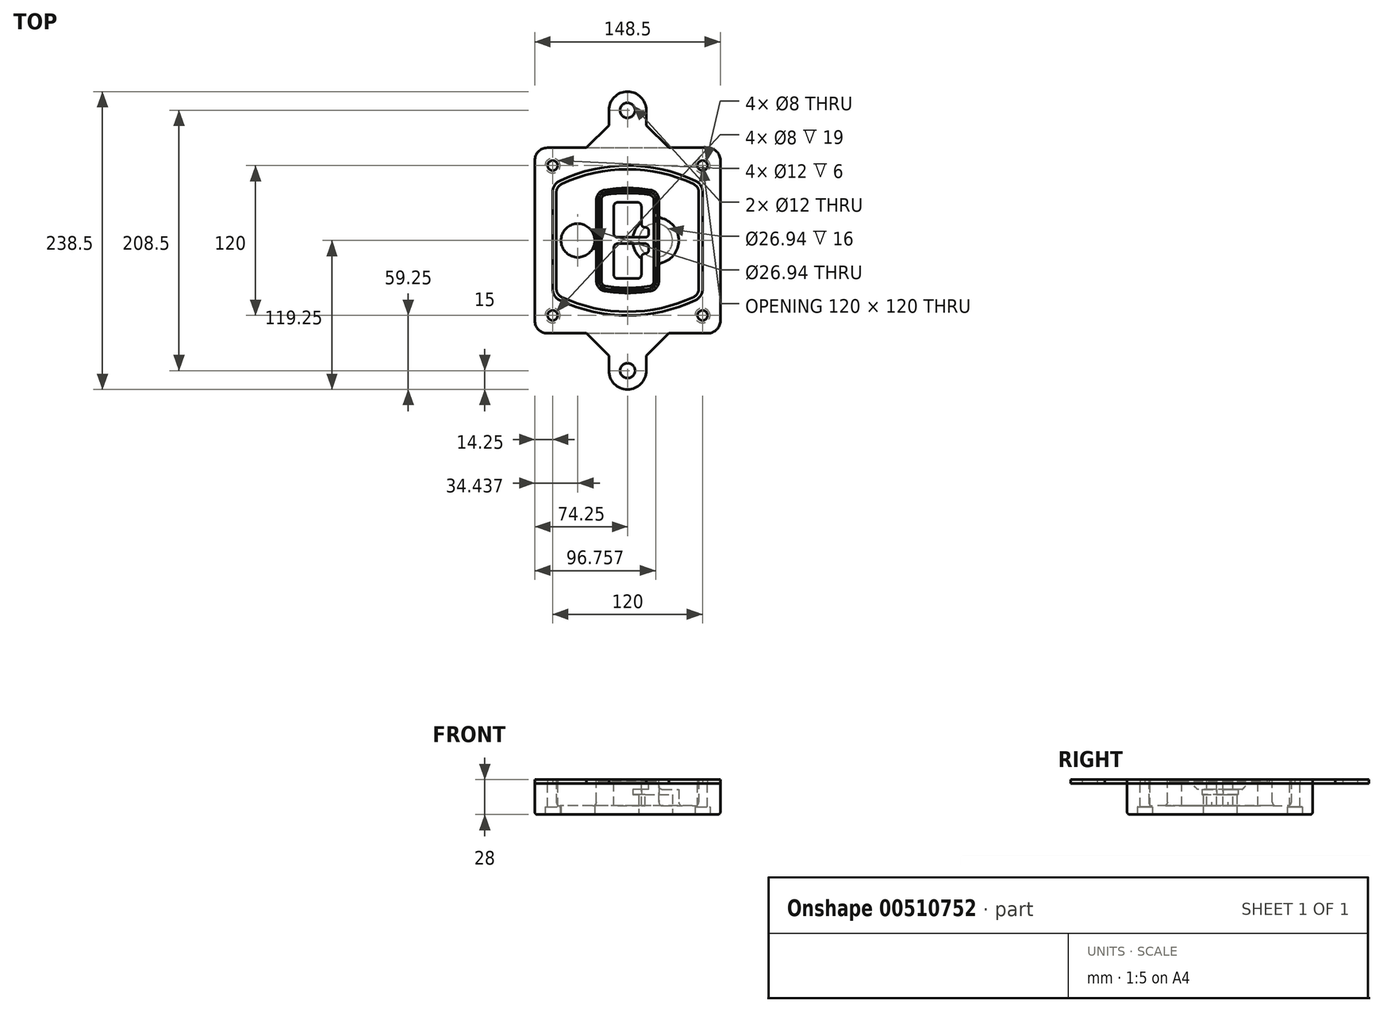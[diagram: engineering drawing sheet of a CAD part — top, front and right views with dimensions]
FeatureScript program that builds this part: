
annotation { "Feature Type Name" : "Feature", "Feature Type Description" : "" }
export const myFeature = defineFeature(function(context is Context, id is Id, definition is map)
    precondition{}
    {
        {
            var Q0;
            Q0=qCreatedBy(makeId("Top.planeOp"),FACE);
            var sketch = newSketch(context, id + "F0", { "sketchPlane" : qUnion([Q0])});
            skPoint(sketch, "E0.rect.middle", {"position": v(0, 0) * mm});
            skLineSegment(sketch, "E1.bottom", {"start": v(-64.25, -74.25) * mm, "end": v(64.25, -74.25) * mm});
            skLineSegment(sketch, "E1.top", {"start": v(-64.25, 74.25) * mm, "end": v(64.25, 74.25) * mm});
            skLineSegment(sketch, "E1.left", {"start": v(-74.25, -64.25) * mm, "end": v(-74.25, 64.25) * mm});
            skLineSegment(sketch, "E1.right", {"start": v(74.25, -64.25) * mm, "end": v(74.25, 64.25) * mm});
            skLineSegment(sketch, "E2", {"start": v(-74.25, 74.25) * mm, "end": v(74.25, -74.25) * mm, "construction": true});
            skLineSegment(sketch, "E3", {"start": v(74.25, 74.25) * mm, "end": v(-74.25, -74.25) * mm, "construction": true});
            skCircle(sketch, "E4", {"center": v(-60, 60) * mm, "radius": 4 * mm});
            skCircle(sketch, "E5", {"center": v(60, 60) * mm, "radius": 4 * mm});
            skCircle(sketch, "E6", {"center": v(60, -60) * mm, "radius": 4 * mm});
            skCircle(sketch, "E7", {"center": v(-60, -60) * mm, "radius": 4 * mm});
            skLineSegment(sketch, "E8", {"start": v(-60, 60) * mm, "end": v(60, 60) * mm, "construction": true});
            skLineSegment(sketch, "E9", {"start": v(60, 60) * mm, "end": v(60, -60) * mm, "construction": true});
            skLineSegment(sketch, "E10", {"start": v(60, -60) * mm, "end": v(-60, -60) * mm, "construction": true});
            skLineSegment(sketch, "E11", {"start": v(-60, -60) * mm, "end": v(-60, 60) * mm, "construction": true});
            skLineSegment(sketch, "E12", {"start": v(-60, 38.83) * mm, "end": v(-60, -38.83) * mm});
            skLineSegment(sketch, "E13", {"start": v(60, 38.83) * mm, "end": v(60, -38.83) * mm});
            skArc(sketch, "E14", {"start": v(54.26, 47.88) * mm, "mid": v(0, 60) * mm, "end": v(-54.26, 47.88) * mm});
            skArc(sketch, "E15", {"start": v(-54.26, -47.88) * mm, "mid": v(0, -60) * mm, "end": v(54.26, -47.88) * mm});
            skLineSegment(sketch, "E16", {"start": v(-60, 0) * mm, "end": v(60, 0) * mm, "construction": true});
            skPoint(sketch, "E17.visualSharp", {"position": v(-60, -45) * mm});
            skArc(sketch, "E17.filletArc", {"start": v(-60, -38.83) * mm, "mid": v(-58.44, -44.2) * mm, "end": v(-54.26, -47.88) * mm});
            skPoint(sketch, "E18.visualSharp", {"position": v(-60, 45) * mm});
            skArc(sketch, "E18.filletArc", {"start": v(-54.26, 47.88) * mm, "mid": v(-58.44, 44.2) * mm, "end": v(-60, 38.83) * mm});
            skPoint(sketch, "E19.visualSharp", {"position": v(60, 45) * mm});
            skArc(sketch, "E19.filletArc", {"start": v(60, 38.83) * mm, "mid": v(58.44, 44.2) * mm, "end": v(54.26, 47.88) * mm});
            skPoint(sketch, "E20.visualSharp", {"position": v(60, -45) * mm});
            skArc(sketch, "E20.filletArc", {"start": v(54.26, -47.88) * mm, "mid": v(58.44, -44.2) * mm, "end": v(60, -38.83) * mm});
            skPoint(sketch, "E21.visualSharp", {"position": v(-74.25, 74.25) * mm});
            skArc(sketch, "E21.filletArc", {"start": v(-64.25, 74.25) * mm, "mid": v(-71.32, 71.32) * mm, "end": v(-74.25, 64.25) * mm});
            skPoint(sketch, "E22.visualSharp", {"position": v(74.25, 74.25) * mm});
            skArc(sketch, "E22.filletArc", {"start": v(74.25, 64.25) * mm, "mid": v(71.32, 71.32) * mm, "end": v(64.25, 74.25) * mm});
            skPoint(sketch, "E23.visualSharp", {"position": v(74.25, -74.25) * mm});
            skArc(sketch, "E23.filletArc", {"start": v(64.25, -74.25) * mm, "mid": v(71.32, -71.32) * mm, "end": v(74.25, -64.25) * mm});
            skPoint(sketch, "E24.visualSharp", {"position": v(-74.25, -74.25) * mm});
            skArc(sketch, "E24.filletArc", {"start": v(-74.25, -64.25) * mm, "mid": v(-71.32, -71.32) * mm, "end": v(-64.25, -74.25) * mm});
            skArc(sketch, "E25.0", {"start": v(57, 38.83) * mm, "mid": v(55.9, 42.58) * mm, "end": v(52.98, 45.17) * mm});
            skLineSegment(sketch, "E25.1", {"start": v(57, 38.83) * mm, "end": v(57, -38.83) * mm});
            skArc(sketch, "E25.2", {"start": v(52.98, -45.17) * mm, "mid": v(55.9, -42.58) * mm, "end": v(57, -38.83) * mm});
            skArc(sketch, "E25.3", {"start": v(-52.98, -45.17) * mm, "mid": v(0, -57) * mm, "end": v(52.98, -45.17) * mm});
            skArc(sketch, "E25.4", {"start": v(-57, -38.83) * mm, "mid": v(-55.9, -42.58) * mm, "end": v(-52.98, -45.17) * mm});
            skArc(sketch, "E25.5", {"start": v(52.98, 45.17) * mm, "mid": v(0, 57) * mm, "end": v(-52.98, 45.17) * mm});
            skLineSegment(sketch, "E25.6", {"start": v(-57, 38.83) * mm, "end": v(-57, -38.83) * mm});
            skArc(sketch, "E25.7", {"start": v(-52.98, 45.17) * mm, "mid": v(-55.9, 42.58) * mm, "end": v(-57, 38.83) * mm});
            skArc(sketch, "E26.0", {"start": v(-55.96, 51.5) * mm, "mid": v(-61.82, 46.33) * mm, "end": v(-64, 38.83) * mm});
            skArc(sketch, "E26.1", {"start": v(55.96, 51.5) * mm, "mid": v(0, 64) * mm, "end": v(-55.96, 51.5) * mm});
            skArc(sketch, "E26.2", {"start": v(64, 38.83) * mm, "mid": v(61.82, 46.33) * mm, "end": v(55.96, 51.5) * mm});
            skLineSegment(sketch, "E26.3", {"start": v(64, 38.83) * mm, "end": v(64, -38.83) * mm});
            skArc(sketch, "E26.4", {"start": v(55.96, -51.5) * mm, "mid": v(61.82, -46.33) * mm, "end": v(64, -38.83) * mm});
            skLineSegment(sketch, "E26.5", {"start": v(-64, 38.83) * mm, "end": v(-64, -38.83) * mm});
            skArc(sketch, "E26.6", {"start": v(-55.96, -51.5) * mm, "mid": v(0, -64) * mm, "end": v(55.96, -51.5) * mm});
            skArc(sketch, "E26.7", {"start": v(-64, -38.83) * mm, "mid": v(-61.82, -46.33) * mm, "end": v(-55.96, -51.5) * mm});
            skSolve(sketch);
        }
        {
            var Q0;
            Q0=makeQuery(id+"F0.imprint","IMPRINT",FACE,{"disambiguationData":[TD([[makeQuery(id+"F0.imprint","IMPRINT",EDGE,{"derivedFrom":sQuery(id+"F0.wireOp",EDGE,"E1.bottom")}),1.0]])]});
            var Q1;
            Q1=makeQuery(id+"F0.imprint","IMPRINT",FACE,{"disambiguationData":[TD([[makeQuery(id+"F0.imprint","IMPRINT",EDGE,{"derivedFrom":sQuery(id+"F0.wireOp",EDGE,"E12")}),1.0]])]});
            var Q2;
            Q2=makeQuery(id+"F0.imprint","IMPRINT",FACE,{"disambiguationData":[TD([[makeQuery(id+"F0.imprint","IMPRINT",EDGE,{"derivedFrom":sQuery(id+"F0.wireOp",EDGE,"E25.0")}),1.0]])]});
            var Q3;
            Q3=makeQuery(id+"F0.imprint","IMPRINT",FACE,{"disambiguationData":[TD([[makeQuery(id+"F0.imprint","IMPRINT",EDGE,{"derivedFrom":sQuery(id+"F0.wireOp",EDGE,"E12")}),-1.0]])]});
            extrude(context, id + "F1", {"entities" : qUnion([Q0, Q1, Q2, Q3]), "oppositeDirection" : true, "depth" : 25 * mm});
        }
        {
            var Q0;
            Q0=makeQuery(id+"F0.imprint","IMPRINT",FACE,{"disambiguationData":[TD([[makeQuery(id+"F0.imprint","IMPRINT",EDGE,{"derivedFrom":sQuery(id+"F0.wireOp",EDGE,"E12")}),1.0]])]});
            extrude(context, id + "F2", {"entities" : qUnion([Q0]), "operationType" : NewBodyOperationType.ADD, "depth" : 3 * mm});
        }
        {
            var Q0;
            Q0=makeQuery(id+"F0.imprint","IMPRINT",FACE,{"disambiguationData":[TD([[makeQuery(id+"F0.imprint","IMPRINT",EDGE,{"derivedFrom":sQuery(id+"F0.wireOp",EDGE,"E25.0")}),1.0]])]});
            extrude(context, id + "F3", {"entities" : qUnion([Q0]), "operationType" : NewBodyOperationType.REMOVE, "oppositeDirection" : true, "depth" : 18 * mm});
        }
        {
            var Q0;
            Q0=makeQuery(id+"F2.opExtrude","CAP_FACE",FACE,{"disambiguationData":[OSD([sQuery(id+"F0.wireOp",EDGE,"E12"),sQuery(id+"F0.wireOp",EDGE,"E13"),sQuery(id+"F0.wireOp",EDGE,"E14"),sQuery(id+"F0.wireOp",EDGE,"E15"),sQuery(id+"F0.wireOp",EDGE,"E17.filletArc"),sQuery(id+"F0.wireOp",EDGE,"E18.filletArc"),sQuery(id+"F0.wireOp",EDGE,"E19.filletArc"),sQuery(id+"F0.wireOp",EDGE,"E20.filletArc"),sQuery(id+"F0.wireOp",EDGE,"E25.0"),sQuery(id+"F0.wireOp",EDGE,"E25.1"),sQuery(id+"F0.wireOp",EDGE,"E25.2"),sQuery(id+"F0.wireOp",EDGE,"E25.3"),sQuery(id+"F0.wireOp",EDGE,"E25.4"),sQuery(id+"F0.wireOp",EDGE,"E25.5"),sQuery(id+"F0.wireOp",EDGE,"E25.6"),sQuery(id+"F0.wireOp",EDGE,"E25.7")])],"isStart":false});
            var sketch = newSketch(context, id + "F4", { "sketchPlane" : qUnion([Q0])});
            skArc(sketch, "E27.0", {"start": v(-18.34, -40.45) * mm, "mid": v(0, -42) * mm, "end": v(18.34, -40.45) * mm});
            skArc(sketch, "E28.0", {"start": v(18.34, 40.45) * mm, "mid": v(0, 42) * mm, "end": v(-18.34, 40.45) * mm});
            skLineSegment(sketch, "E29", {"start": v(-25, 32.57) * mm, "end": v(-25, -32.57) * mm});
            skLineSegment(sketch, "E30", {"start": v(25, 32.57) * mm, "end": v(25, -32.57) * mm});
            skLineSegment(sketch, "E31", {"start": v(-25, 39.1) * mm, "end": v(25, 39.1) * mm, "construction": true});
            skLineSegment(sketch, "E32", {"start": v(-25, -39.1) * mm, "end": v(25, -39.1) * mm, "construction": true});
            skPoint(sketch, "E33.visualSharp", {"position": v(-25, 39.1) * mm});
            skArc(sketch, "E33.filletArc", {"start": v(-18.34, 40.45) * mm, "mid": v(-23.11, 37.73) * mm, "end": v(-25, 32.57) * mm});
            skPoint(sketch, "E34.visualSharp", {"position": v(25, 39.1) * mm});
            skArc(sketch, "E34.filletArc", {"start": v(25, 32.57) * mm, "mid": v(23.11, 37.73) * mm, "end": v(18.34, 40.45) * mm});
            skPoint(sketch, "E35.visualSharp", {"position": v(25, -39.1) * mm});
            skArc(sketch, "E35.filletArc", {"start": v(18.34, -40.45) * mm, "mid": v(23.11, -37.73) * mm, "end": v(25, -32.57) * mm});
            skPoint(sketch, "E36.visualSharp", {"position": v(-25, -39.1) * mm});
            skArc(sketch, "E36.filletArc", {"start": v(-25, -32.57) * mm, "mid": v(-23.11, -37.73) * mm, "end": v(-18.34, -40.45) * mm});
            skArc(sketch, "E37.0", {"start": v(52.98, 45.17) * mm, "mid": v(0, 57) * mm, "end": v(-52.98, 45.17) * mm});
            skArc(sketch, "E37.1", {"start": v(-52.98, 45.17) * mm, "mid": v(-55.9, 42.58) * mm, "end": v(-57, 38.83) * mm});
            skLineSegment(sketch, "E37.2", {"start": v(-57, 38.83) * mm, "end": v(-57, -38.83) * mm});
            skArc(sketch, "E37.3", {"start": v(-57, -38.83) * mm, "mid": v(-55.9, -42.58) * mm, "end": v(-52.98, -45.17) * mm});
            skArc(sketch, "E37.4", {"start": v(-52.98, -45.17) * mm, "mid": v(0, -57) * mm, "end": v(52.98, -45.17) * mm});
            skArc(sketch, "E37.5", {"start": v(52.98, -45.17) * mm, "mid": v(55.9, -42.58) * mm, "end": v(57, -38.83) * mm});
            skLineSegment(sketch, "E37.6", {"start": v(57, 38.83) * mm, "end": v(57, -38.83) * mm});
            skArc(sketch, "E37.7", {"start": v(57, 38.83) * mm, "mid": v(55.9, 42.58) * mm, "end": v(52.98, 45.17) * mm});
            skLineSegment(sketch, "E38.0", {"start": v(23, 32.57) * mm, "end": v(23, -32.57) * mm});
            skArc(sketch, "E38.1", {"start": v(18, -38.48) * mm, "mid": v(21.58, -36.44) * mm, "end": v(23, -32.57) * mm});
            skArc(sketch, "E38.2", {"start": v(-18, -38.48) * mm, "mid": v(0, -40) * mm, "end": v(18, -38.48) * mm});
            skArc(sketch, "E38.3", {"start": v(-23, -32.57) * mm, "mid": v(-21.58, -36.44) * mm, "end": v(-18, -38.48) * mm});
            skLineSegment(sketch, "E38.4", {"start": v(-23, 32.57) * mm, "end": v(-23, -32.57) * mm});
            skArc(sketch, "E38.5", {"start": v(23, 32.57) * mm, "mid": v(21.58, 36.44) * mm, "end": v(18, 38.48) * mm});
            skArc(sketch, "E38.6", {"start": v(-18, 38.48) * mm, "mid": v(-21.58, 36.44) * mm, "end": v(-23, 32.57) * mm});
            skArc(sketch, "E38.7", {"start": v(18, 38.48) * mm, "mid": v(0, 40) * mm, "end": v(-18, 38.48) * mm});
            skArc(sketch, "E39.0", {"start": v(21, 32.57) * mm, "mid": v(20.06, 35.15) * mm, "end": v(17.67, 36.5) * mm});
            skLineSegment(sketch, "E39.1", {"start": v(21, 32.57) * mm, "end": v(21, -32.57) * mm});
            skArc(sketch, "E39.2", {"start": v(17.67, -36.5) * mm, "mid": v(20.06, -35.15) * mm, "end": v(21, -32.57) * mm});
            skArc(sketch, "E39.3", {"start": v(-17.67, -36.5) * mm, "mid": v(0, -38) * mm, "end": v(17.67, -36.5) * mm});
            skArc(sketch, "E39.4", {"start": v(-21, -32.57) * mm, "mid": v(-20.06, -35.15) * mm, "end": v(-17.67, -36.5) * mm});
            skArc(sketch, "E39.5", {"start": v(17.67, 36.5) * mm, "mid": v(0, 38) * mm, "end": v(-17.67, 36.5) * mm});
            skLineSegment(sketch, "E39.6", {"start": v(-21, 32.57) * mm, "end": v(-21, -32.57) * mm});
            skArc(sketch, "E39.7", {"start": v(-17.67, 36.5) * mm, "mid": v(-20.06, 35.15) * mm, "end": v(-21, 32.57) * mm});
            skLineSegment(sketch, "E40", {"start": v(-25, 0) * mm, "end": v(25, 0) * mm, "construction": true});
            skLineSegment(sketch, "E41", {"start": v(-11, 5.5) * mm, "end": v(-11, 27.5) * mm});
            skLineSegment(sketch, "E42", {"start": v(-8, 30.5) * mm, "end": v(8, 30.5) * mm});
            skLineSegment(sketch, "E43", {"start": v(11, 27.5) * mm, "end": v(11, 13.5) * mm});
            skLineSegment(sketch, "E44", {"start": v(14, 10.5) * mm, "end": v(14, 10.5) * mm});
            skLineSegment(sketch, "E45", {"start": v(17, 7.5) * mm, "end": v(17, 5.5) * mm});
            skLineSegment(sketch, "E46", {"start": v(14, 2.5) * mm, "end": v(-8, 2.5) * mm});
            skPoint(sketch, "E47.visualSharp", {"position": v(-11, 30.5) * mm});
            skArc(sketch, "E47.filletArc", {"start": v(-8, 30.5) * mm, "mid": v(-10.12, 29.62) * mm, "end": v(-11, 27.5) * mm});
            skPoint(sketch, "E48.visualSharp", {"position": v(11, 30.5) * mm});
            skArc(sketch, "E48.filletArc", {"start": v(11, 27.5) * mm, "mid": v(10.12, 29.62) * mm, "end": v(8, 30.5) * mm});
            skPoint(sketch, "E49.visualSharp", {"position": v(11, 10.5) * mm});
            skArc(sketch, "E49.filletArc", {"start": v(11, 13.5) * mm, "mid": v(11.88, 11.38) * mm, "end": v(14, 10.5) * mm});
            skPoint(sketch, "E50.visualSharp", {"position": v(17, 10.5) * mm});
            skArc(sketch, "E50.filletArc", {"start": v(17, 7.5) * mm, "mid": v(16.12, 9.62) * mm, "end": v(14, 10.5) * mm});
            skPoint(sketch, "E51.visualSharp", {"position": v(17, 2.5) * mm});
            skArc(sketch, "E51.filletArc", {"start": v(14, 2.5) * mm, "mid": v(16.12, 3.38) * mm, "end": v(17, 5.5) * mm});
            skPoint(sketch, "E52.visualSharp", {"position": v(-11, 2.5) * mm});
            skArc(sketch, "E52.filletArc", {"start": v(-11, 5.5) * mm, "mid": v(-10.12, 3.38) * mm, "end": v(-8, 2.5) * mm});
            skLineSegment(sketch, "E53.0.MirrorCS", {"start": v(14, -2.5) * mm, "end": v(-8, -2.5) * mm});
            skArc(sketch, "E54.0.MirrorCS", {"start": v(-11, -5.5) * mm, "mid": v(-10.12, -3.38) * mm, "end": v(-8, -2.5) * mm});
            skLineSegment(sketch, "E55.0.MirrorCS", {"start": v(-11, -5.5) * mm, "end": v(-11, -27.5) * mm});
            skArc(sketch, "E56.0.MirrorCS", {"start": v(-8, -30.5) * mm, "mid": v(-10.12, -29.62) * mm, "end": v(-11, -27.5) * mm});
            skLineSegment(sketch, "E57.0.MirrorCS", {"start": v(-8, -30.5) * mm, "end": v(8, -30.5) * mm});
            skArc(sketch, "E58.0.MirrorCS", {"start": v(11, -27.5) * mm, "mid": v(10.12, -29.62) * mm, "end": v(8, -30.5) * mm});
            skLineSegment(sketch, "E59.0.MirrorCS", {"start": v(11, -27.5) * mm, "end": v(11, -13.5) * mm});
            skArc(sketch, "E60.0.MirrorCS", {"start": v(11, -13.5) * mm, "mid": v(11.88, -11.38) * mm, "end": v(14, -10.5) * mm});
            skArc(sketch, "E61.0.MirrorCS", {"start": v(17, -7.5) * mm, "mid": v(16.12, -9.62) * mm, "end": v(14, -10.5) * mm});
            skLineSegment(sketch, "E62.0.MirrorCS", {"start": v(17, -7.5) * mm, "end": v(17, -5.5) * mm});
            skArc(sketch, "E63.0.MirrorCS", {"start": v(14, -2.5) * mm, "mid": v(16.12, -3.38) * mm, "end": v(17, -5.5) * mm});
            skSolve(sketch);
        }
        {
            var Q0;
            Q0=makeQuery(id+"F4.imprint","IMPRINT",FACE,{"disambiguationData":[TD([[makeQuery(id+"F4.imprint","IMPRINT",EDGE,{"derivedFrom":sQuery(id+"F4.wireOp",EDGE,"E27.0")}),1.0]])]});
            var Q1;
            Q1=makeQuery(id+"F4.imprint","IMPRINT",FACE,{"disambiguationData":[TD([[makeQuery(id+"F4.imprint","IMPRINT",EDGE,{"derivedFrom":sQuery(id+"F4.wireOp",EDGE,"E38.0")}),-1.0]])]});
            var Q2;
            Q2=makeQuery(id+"F4.imprint","IMPRINT",FACE,{"disambiguationData":[TD([[makeQuery(id+"F4.imprint","IMPRINT",EDGE,{"derivedFrom":sQuery(id+"F4.wireOp",EDGE,"E39.0")}),1.0]])]});
            extrude(context, id + "F5", {"entities" : qUnion([Q0, Q1, Q2]), "operationType" : NewBodyOperationType.ADD, "endBound" : BoundingType.UP_TO_NEXT, "oppositeDirection" : true, "depth" : 25 * mm});
        }
        {
            var Q0;
            Q0=makeQuery(id+"F4.imprint","IMPRINT",FACE,{"disambiguationData":[TD([[makeQuery(id+"F4.imprint","IMPRINT",EDGE,{"derivedFrom":sQuery(id+"F4.wireOp",EDGE,"E38.0")}),-1.0]])]});
            extrude(context, id + "F6", {"entities" : qUnion([Q0]), "operationType" : NewBodyOperationType.REMOVE, "oppositeDirection" : true, "depth" : 2 * mm});
        }
        {
            var Q0;
            Q0=makeQuery(id+"F1.opExtrude","CAP_FACE",FACE,{"disambiguationData":[OSD([sQuery(id+"F0.wireOp",EDGE,"E1.bottom"),sQuery(id+"F0.wireOp",EDGE,"E1.top"),sQuery(id+"F0.wireOp",EDGE,"E1.left"),sQuery(id+"F0.wireOp",EDGE,"E1.right"),sQuery(id+"F0.wireOp",EDGE,"E4"),sQuery(id+"F0.wireOp",EDGE,"E5"),sQuery(id+"F0.wireOp",EDGE,"E6"),sQuery(id+"F0.wireOp",EDGE,"E7"),sQuery(id+"F0.wireOp",EDGE,"E21.filletArc"),sQuery(id+"F0.wireOp",EDGE,"E22.filletArc"),sQuery(id+"F0.wireOp",EDGE,"E23.filletArc"),sQuery(id+"F0.wireOp",EDGE,"E24.filletArc")])],"isStart":false});
            var sketch = newSketch(context, id + "F7", { "sketchPlane" : qUnion([Q0])});
            skCircle(sketch, "E64", {"center": v(22.5, 0) * mm, "radius": 13.47 * mm});
            skCircle(sketch, "E65", {"center": v(-39.81, 0) * mm, "radius": 13.47 * mm});
            skLineSegment(sketch, "E66", {"start": v(74.25, 0) * mm, "end": v(-74.25, 0) * mm});
            skCircle(sketch, "E67", {"center": v(22.5, 0) * mm, "radius": 18.47 * mm});
            skCircle(sketch, "E68", {"center": v(60, -60) * mm, "radius": 6 * mm});
            skCircle(sketch, "E69", {"center": v(-60, -60) * mm, "radius": 6 * mm});
            skCircle(sketch, "E70", {"center": v(-60, 60) * mm, "radius": 6 * mm});
            skCircle(sketch, "E71", {"center": v(60, 60) * mm, "radius": 6 * mm});
            skSolve(sketch);
        }
        {
            var Q0;
            {var subQ1=sQuery(id+"F7.wireOp",EDGE,"E66");var subQ4=sQuery(id+"F7.wireOp",EDGE,"E64");var subQ6=makeQuery(id+"F7.imprint","INTERSECT",VERTEX,{"disambiguationData":[OD(0.0)],"derivedFrom":[subQ4,subQ1]});Q0=makeQuery(id+"F7.imprint","IMPRINT",FACE,{"disambiguationData":[TD([[makeQuery(id+"F7.imprint","IMPRINT",EDGE,{"disambiguationData":[TD([[subQ6,-1.0]])],"derivedFrom":subQ4}),-1.0]])]});}
            var Q1;
            {var subQ0=sQuery(id+"F7.wireOp",EDGE,"E66");var subQ1=sQuery(id+"F7.wireOp",EDGE,"E64");var subQ3=makeQuery(id+"F7.imprint","INTERSECT",VERTEX,{"disambiguationData":[OD(0.0)],"derivedFrom":[subQ1,subQ0]});Q1=makeQuery(id+"F7.imprint","IMPRINT",FACE,{"disambiguationData":[TD([[makeQuery(id+"F7.imprint","IMPRINT",EDGE,{"disambiguationData":[TD([[subQ3,-1.0]])],"derivedFrom":subQ1}),1.0]])]});}
            var Q2;
            {var subQ0=sQuery(id+"F7.wireOp",EDGE,"E66");var subQ1=sQuery(id+"F7.wireOp",EDGE,"E64");var subQ3=makeQuery(id+"F7.imprint","INTERSECT",VERTEX,{"disambiguationData":[OD(0.0)],"derivedFrom":[subQ1,subQ0]});Q2=makeQuery(id+"F7.imprint","IMPRINT",FACE,{"disambiguationData":[TD([[makeQuery(id+"F7.imprint","IMPRINT",EDGE,{"disambiguationData":[TD([[subQ3,1.0]])],"derivedFrom":subQ1}),1.0]])]});}
            var Q3;
            {var subQ1=sQuery(id+"F7.wireOp",EDGE,"E66");var subQ4=sQuery(id+"F7.wireOp",EDGE,"E64");var subQ6=makeQuery(id+"F7.imprint","INTERSECT",VERTEX,{"disambiguationData":[OD(0.0)],"derivedFrom":[subQ4,subQ1]});Q3=makeQuery(id+"F7.imprint","IMPRINT",FACE,{"disambiguationData":[TD([[makeQuery(id+"F7.imprint","IMPRINT",EDGE,{"disambiguationData":[TD([[subQ6,1.0]])],"derivedFrom":subQ4}),-1.0]])]});}
            extrude(context, id + "F8", {"entities" : qUnion([Q0, Q1, Q2, Q3]), "operationType" : NewBodyOperationType.ADD, "oppositeDirection" : true, "depth" : 20 * mm});
        }
        {
            var Q0;
            {var subQ0=sQuery(id+"F7.wireOp",EDGE,"E66");var subQ1=sQuery(id+"F7.wireOp",EDGE,"E64");var subQ3=makeQuery(id+"F7.imprint","INTERSECT",VERTEX,{"disambiguationData":[OD(0.0)],"derivedFrom":[subQ1,subQ0]});Q0=makeQuery(id+"F7.imprint","IMPRINT",FACE,{"disambiguationData":[TD([[makeQuery(id+"F7.imprint","IMPRINT",EDGE,{"disambiguationData":[TD([[subQ3,-1.0]])],"derivedFrom":subQ1}),1.0]])]});}
            var Q1;
            {var subQ0=sQuery(id+"F7.wireOp",EDGE,"E66");var subQ1=sQuery(id+"F7.wireOp",EDGE,"E64");var subQ3=makeQuery(id+"F7.imprint","INTERSECT",VERTEX,{"disambiguationData":[OD(0.0)],"derivedFrom":[subQ1,subQ0]});Q1=makeQuery(id+"F7.imprint","IMPRINT",FACE,{"disambiguationData":[TD([[makeQuery(id+"F7.imprint","IMPRINT",EDGE,{"disambiguationData":[TD([[subQ3,1.0]])],"derivedFrom":subQ1}),1.0]])]});}
            extrude(context, id + "F9", {"entities" : qUnion([Q0, Q1]), "operationType" : NewBodyOperationType.REMOVE, "oppositeDirection" : true, "depth" : 16 * mm});
        }
        {
            var Q0;
            {var subQ0=sQuery(id+"F7.wireOp",EDGE,"E66");var subQ1=sQuery(id+"F7.wireOp",EDGE,"E65");var subQ3=makeQuery(id+"F7.imprint","INTERSECT",VERTEX,{"disambiguationData":[OD(0.0)],"derivedFrom":[subQ1,subQ0]});Q0=makeQuery(id+"F7.imprint","IMPRINT",FACE,{"disambiguationData":[TD([[makeQuery(id+"F7.imprint","IMPRINT",EDGE,{"disambiguationData":[TD([[subQ3,-1.0]])],"derivedFrom":subQ1}),1.0]])]});}
            var Q1;
            {var subQ0=sQuery(id+"F7.wireOp",EDGE,"E66");var subQ1=sQuery(id+"F7.wireOp",EDGE,"E65");var subQ3=makeQuery(id+"F7.imprint","INTERSECT",VERTEX,{"disambiguationData":[OD(0.0)],"derivedFrom":[subQ1,subQ0]});Q1=makeQuery(id+"F7.imprint","IMPRINT",FACE,{"disambiguationData":[TD([[makeQuery(id+"F7.imprint","IMPRINT",EDGE,{"disambiguationData":[TD([[subQ3,1.0]])],"derivedFrom":subQ1}),1.0]])]});}
            extrude(context, id + "F10", {"entities" : qUnion([Q0, Q1]), "operationType" : NewBodyOperationType.REMOVE, "oppositeDirection" : true, "depth" : 25 * mm});
        }
        {
            var Q0;
            Q0=makeQuery(id+"F7.imprint","IMPRINT",FACE,{"disambiguationData":[TD([[makeQuery(id+"F7.imprint","IMPRINT",EDGE,{"derivedFrom":sQuery(id+"F7.wireOp",EDGE,"E68")}),1.0]])]});
            var Q1;
            Q1=makeQuery(id+"F7.imprint","IMPRINT",FACE,{"disambiguationData":[TD([[makeQuery(id+"F7.imprint","IMPRINT",EDGE,{"derivedFrom":makeQuery(id+"F1.opExtrude","CAP_EDGE",EDGE,{"disambiguationData":[OSD([sQuery(id+"F0.wireOp",EDGE,"E5")])],"isStart":false})}),-1.0]])]});
            var Q2;
            Q2=makeQuery(id+"F7.imprint","IMPRINT",FACE,{"disambiguationData":[TD([[makeQuery(id+"F7.imprint","IMPRINT",EDGE,{"derivedFrom":sQuery(id+"F7.wireOp",EDGE,"E69")}),1.0]])]});
            var Q3;
            Q3=makeQuery(id+"F7.imprint","IMPRINT",FACE,{"disambiguationData":[TD([[makeQuery(id+"F7.imprint","IMPRINT",EDGE,{"derivedFrom":makeQuery(id+"F1.opExtrude","CAP_EDGE",EDGE,{"disambiguationData":[OSD([sQuery(id+"F0.wireOp",EDGE,"E4")])],"isStart":false})}),-1.0]])]});
            var Q4;
            Q4=makeQuery(id+"F7.imprint","IMPRINT",FACE,{"disambiguationData":[TD([[makeQuery(id+"F7.imprint","IMPRINT",EDGE,{"derivedFrom":sQuery(id+"F7.wireOp",EDGE,"E70")}),1.0]])]});
            var Q5;
            Q5=makeQuery(id+"F7.imprint","IMPRINT",FACE,{"disambiguationData":[TD([[makeQuery(id+"F7.imprint","IMPRINT",EDGE,{"derivedFrom":makeQuery(id+"F1.opExtrude","CAP_EDGE",EDGE,{"disambiguationData":[OSD([sQuery(id+"F0.wireOp",EDGE,"E7")])],"isStart":false})}),-1.0]])]});
            var Q6;
            Q6=makeQuery(id+"F7.imprint","IMPRINT",FACE,{"disambiguationData":[TD([[makeQuery(id+"F7.imprint","IMPRINT",EDGE,{"derivedFrom":sQuery(id+"F7.wireOp",EDGE,"E71")}),1.0]])]});
            var Q7;
            Q7=makeQuery(id+"F7.imprint","IMPRINT",FACE,{"disambiguationData":[TD([[makeQuery(id+"F7.imprint","IMPRINT",EDGE,{"derivedFrom":makeQuery(id+"F1.opExtrude","CAP_EDGE",EDGE,{"disambiguationData":[OSD([sQuery(id+"F0.wireOp",EDGE,"E6")])],"isStart":false})}),-1.0]])]});
            extrude(context, id + "F11", {"entities" : qUnion([Q0, Q1, Q2, Q3, Q4, Q5, Q6, Q7]), "operationType" : NewBodyOperationType.REMOVE, "oppositeDirection" : true, "depth" : 6 * mm});
        }
        {
            var Q0;
            Q0=makeQuery(id+"F9.boolean.opBoolean","COPY",FACE,{"derivedFrom":makeQuery(id+"F9.opExtrude","CAP_FACE",FACE,{"disambiguationData":[OSD([sQuery(id+"F7.wireOp",EDGE,"E64")])],"isStart":false})});
            var sketch = newSketch(context, id + "F12", { "sketchPlane" : qUnion([Q0])});
            skArc(sketch, "E72.0", {"start": v(11, 14.45) * mm, "mid": v(6.45, 9.13) * mm, "end": v(4.2, 2.5) * mm});
            skArc(sketch, "E72.1", {"start": v(4.2, -2.5) * mm, "mid": v(6.45, -9.13) * mm, "end": v(11, -14.45) * mm});
            skLineSegment(sketch, "E73", {"start": v(4.2, -2.5) * mm, "end": v(14, -2.5) * mm});
            skLineSegment(sketch, "E74.0", {"start": v(14, 2.5) * mm, "end": v(4.2, 2.5) * mm});
            skArc(sketch, "E74.1", {"start": v(14, 2.5) * mm, "mid": v(16.12, 3.38) * mm, "end": v(17, 5.5) * mm});
            skLineSegment(sketch, "E74.2", {"start": v(17, 7.5) * mm, "end": v(17, 5.5) * mm});
            skArc(sketch, "E74.3", {"start": v(17, 7.5) * mm, "mid": v(16.12, 9.62) * mm, "end": v(14, 10.5) * mm});
            skArc(sketch, "E74.4", {"start": v(11, 13.5) * mm, "mid": v(11.88, 11.38) * mm, "end": v(14, 10.5) * mm});
            skLineSegment(sketch, "E74.5", {"start": v(11, 14.45) * mm, "end": v(11, 13.5) * mm});
            skLineSegment(sketch, "E74.7", {"start": v(14, -2.5) * mm, "end": v(4.2, -2.5) * mm});
            skArc(sketch, "E74.8", {"start": v(14, -2.5) * mm, "mid": v(16.12, -3.38) * mm, "end": v(17, -5.5) * mm});
            skLineSegment(sketch, "E74.9", {"start": v(17, -7.5) * mm, "end": v(17, -5.5) * mm});
            skArc(sketch, "E74.10", {"start": v(17, -7.5) * mm, "mid": v(16.12, -9.62) * mm, "end": v(14, -10.5) * mm});
            skArc(sketch, "E74.11", {"start": v(11, -13.5) * mm, "mid": v(11.88, -11.38) * mm, "end": v(14, -10.5) * mm});
            skLineSegment(sketch, "E74.12", {"start": v(11, -14.45) * mm, "end": v(11, -13.5) * mm});
            skPoint(sketch, "E75.orphan", {"position": v(11, -27.5) * mm});
            skPoint(sketch, "E76.orphan", {"position": v(-8, -2.5) * mm});
            skPoint(sketch, "E77.orphan", {"position": v(-8, 2.5) * mm});
            skPoint(sketch, "E78.orphan", {"position": v(11, 27.5) * mm});
            skSolve(sketch);
        }
        {
            var Q0;
            {var subQ7=sQuery(id+"F12.wireOp",EDGE,"E72.0");var subQ14=sQuery(id+"F12.wireOp",EDGE,"E72.1");var subQ16=sQuery(id+"F12.wireOp",EDGE,"E74.1");var subQ18=sQuery(id+"F12.wireOp",EDGE,"E74.8");Q0=qUnion([makeQuery(id+"F12.imprint","IMPRINT",FACE,{"disambiguationData":[TD([[makeQuery(id+"F12.imprint","IMPRINT",EDGE,{"derivedFrom":subQ7}),1.0]])]}),makeQuery(id+"F12.imprint","IMPRINT",FACE,{"disambiguationData":[TD([[makeQuery(id+"F12.imprint","IMPRINT",EDGE,{"derivedFrom":subQ14}),1.0]])]}),makeQuery(id+"F12.imprint","IMPRINT",FACE,{"disambiguationData":[TD([[makeQuery(id+"F12.imprint","IMPRINT",EDGE,{"derivedFrom":subQ16}),1.0]])]}),makeQuery(id+"F12.imprint","IMPRINT",FACE,{"disambiguationData":[TD([[makeQuery(id+"F12.imprint","IMPRINT",EDGE,{"derivedFrom":subQ18}),-1.0]])]})]);}
            var Q1;
            Q1=makeQuery(id+"F5.boolean.opBoolean","SPLIT",FACE,{"disambiguationData":[TD([makeQuery(id+"F5.opExtrude","SWEPT_FACE",FACE,{"disambiguationData":[OSD([sQuery(id+"F4.wireOp",EDGE,"E41")])]})])],"derivedFrom":makeQuery(id+"F3.boolean.opBoolean","COPY",FACE,{"derivedFrom":makeQuery(id+"F3.opExtrude","CAP_FACE",FACE,{"disambiguationData":[OSD([sQuery(id+"F0.wireOp",EDGE,"E25.0"),sQuery(id+"F0.wireOp",EDGE,"E25.1"),sQuery(id+"F0.wireOp",EDGE,"E25.2"),sQuery(id+"F0.wireOp",EDGE,"E25.3"),sQuery(id+"F0.wireOp",EDGE,"E25.4"),sQuery(id+"F0.wireOp",EDGE,"E25.5"),sQuery(id+"F0.wireOp",EDGE,"E25.6"),sQuery(id+"F0.wireOp",EDGE,"E25.7")])],"isStart":false})})});
            extrude(context, id + "F13", {"entities" : qUnion([Q0]), "operationType" : NewBodyOperationType.REMOVE, "endBound" : BoundingType.UP_TO_SURFACE, "endBoundEntityFace" : qUnion([Q1]), "depth" : 25 * mm});
        }
        {
            var Q0;
            Q0=makeQuery(id+"F3.boolean.opBoolean","COPY",EDGE,{"derivedFrom":makeQuery(id+"F3.opExtrude","CAP_EDGE",EDGE,{"disambiguationData":[OSD([sQuery(id+"F0.wireOp",EDGE,"E25.6")])],"isStart":false})});
            var Q1;
            Q1=makeQuery(id+"F8.boolean.opBoolean","INTERSECT",EDGE,{"derivedFrom":[makeQuery(id+"F5.opExtrude","SWEPT_FACE",FACE,{"disambiguationData":[OSD([sQuery(id+"F4.wireOp",EDGE,"E30")])]}),makeQuery(id+"F8.opExtrude","CAP_FACE",FACE,{"disambiguationData":[OSD([sQuery(id+"F7.wireOp",EDGE,"E67")])],"isStart":false})]});
            var Q2;
            Q2=makeQuery(id+"F8.boolean.opBoolean","INTERSECT",EDGE,{"disambiguationData":[OD(1.0)],"derivedFrom":[makeQuery(id+"F5.opExtrude","SWEPT_FACE",FACE,{"disambiguationData":[OSD([sQuery(id+"F4.wireOp",EDGE,"E30")])]}),makeQuery(id+"F8.opExtrude","SWEPT_FACE",FACE,{"disambiguationData":[OSD([sQuery(id+"F7.wireOp",EDGE,"E67")])]})]});
            var Q3;
            {var subQ0=sQuery(id+"F4.wireOp",EDGE,"E30");Q3=makeQuery(id+"F8.boolean.opBoolean","SPLIT",EDGE,{"disambiguationData":[TD([makeQuery(id+"F5.opExtrude","SWEPT_FACE",FACE,{"disambiguationData":[OSD([sQuery(id+"F4.wireOp",EDGE,"E35.filletArc")])]})])],"derivedFrom":makeQuery(id+"F5.opExtrude","CAP_EDGE",EDGE,{"disambiguationData":[OSD([subQ0])],"isStart":false})});}
            var Q4;
            {var subQ0=sQuery(id+"F0.wireOp",EDGE,"E25.7");var subQ1=sQuery(id+"F0.wireOp",EDGE,"E25.1");var subQ2=sQuery(id+"F0.wireOp",EDGE,"E25.6");var subQ3=sQuery(id+"F0.wireOp",EDGE,"E25.5");var subQ4=sQuery(id+"F0.wireOp",EDGE,"E25.4");var subQ5=sQuery(id+"F0.wireOp",EDGE,"E25.0");var subQ6=sQuery(id+"F0.wireOp",EDGE,"E25.2");var subQ7=sQuery(id+"F0.wireOp",EDGE,"E25.3");Q4=makeQuery(id+"F8.boolean.opBoolean","INTERSECT",EDGE,{"derivedFrom":[makeQuery(id+"F5.boolean.opBoolean","SPLIT",FACE,{"disambiguationData":[TD([makeQuery(id+"F2.opExtrude","SWEPT_FACE",FACE,{"disambiguationData":[OSD([subQ5])]})])],"derivedFrom":makeQuery(id+"F3.boolean.opBoolean","COPY",FACE,{"derivedFrom":makeQuery(id+"F3.opExtrude","CAP_FACE",FACE,{"disambiguationData":[OSD([subQ5,subQ1,subQ6,subQ7,subQ4,subQ3,subQ2,subQ0])],"isStart":false})})}),makeQuery(id+"F8.opExtrude","SWEPT_FACE",FACE,{"disambiguationData":[OSD([sQuery(id+"F7.wireOp",EDGE,"E67")])]})]});}
            var Q5;
            Q5=makeQuery(id+"F8.boolean.opBoolean","INTERSECT",EDGE,{"disambiguationData":[OD(0.0)],"derivedFrom":[makeQuery(id+"F5.opExtrude","SWEPT_FACE",FACE,{"disambiguationData":[OSD([sQuery(id+"F4.wireOp",EDGE,"E30")])]}),makeQuery(id+"F8.opExtrude","SWEPT_FACE",FACE,{"disambiguationData":[OSD([sQuery(id+"F7.wireOp",EDGE,"E67")])]})]});
            fillet(context, id + "F14", {"entities" : qUnion([Q0, Q1, Q2, Q3, Q4, Q5]), "radius" : 3 * mm, "tangentPropagation" : true, "allowEdgeOverflow" : false});
        }
        {
            var Q0;
            Q0=makeQuery(id+"F1.opExtrude","CAP_EDGE",EDGE,{"disambiguationData":[OSD([sQuery(id+"F0.wireOp",EDGE,"E1.bottom")])],"isStart":false});
            fillet(context, id + "F15", {"entities" : qUnion([Q0]), "radius" : 2 * mm, "tangentPropagation" : true, "allowEdgeOverflow" : false});
        }
        {
            var Q0;
            {var subQ0=sQuery(id+"F0.wireOp",EDGE,"E21.filletArc");var subQ1=sQuery(id+"F0.wireOp",EDGE,"E7");var subQ2=sQuery(id+"F0.wireOp",EDGE,"E6");var subQ3=sQuery(id+"F0.wireOp",EDGE,"E5");var subQ4=sQuery(id+"F0.wireOp",EDGE,"E4");var subQ5=sQuery(id+"F0.wireOp",EDGE,"E22.filletArc");var subQ6=sQuery(id+"F0.wireOp",EDGE,"E1.bottom");var subQ7=sQuery(id+"F0.wireOp",EDGE,"E1.right");var subQ8=sQuery(id+"F0.wireOp",EDGE,"E1.top");var subQ9=sQuery(id+"F0.wireOp",EDGE,"E1.left");var subQ10=sQuery(id+"F0.wireOp",EDGE,"E23.filletArc");var subQ11=sQuery(id+"F0.wireOp",EDGE,"E24.filletArc");Q0=makeQuery(id+"F2.boolean.opBoolean","SPLIT",FACE,{"disambiguationData":[TD([makeQuery(id+"F1.opExtrude","SWEPT_FACE",FACE,{"disambiguationData":[OSD([subQ6])]})])],"derivedFrom":makeQuery(id+"F1.opExtrude","CAP_FACE",FACE,{"disambiguationData":[OSD([subQ6,subQ8,subQ9,subQ7,subQ4,subQ3,subQ2,subQ1,subQ0,subQ5,subQ10,subQ11])],"isStart":true})});}
            var sketch = newSketch(context, id + "F16", { "sketchPlane" : qUnion([Q0])});
            skLineSegment(sketch, "E79.0", {"start": v(-74.25, -64.25) * mm, "end": v(-74.25, 64.25) * mm});
            skArc(sketch, "E79.1", {"start": v(-74.25, -64.25) * mm, "mid": v(-71.32, -71.32) * mm, "end": v(-64.25, -74.25) * mm});
            skLineSegment(sketch, "E79.2", {"start": v(-64.25, -74.25) * mm, "end": v(64.25, -74.25) * mm});
            skArc(sketch, "E79.3", {"start": v(64.25, -74.25) * mm, "mid": v(71.32, -71.32) * mm, "end": v(74.25, -64.25) * mm});
            skLineSegment(sketch, "E79.4", {"start": v(74.25, -64.25) * mm, "end": v(74.25, 64.25) * mm});
            skArc(sketch, "E79.5", {"start": v(74.25, 64.25) * mm, "mid": v(71.32, 71.32) * mm, "end": v(64.25, 74.25) * mm});
            skArc(sketch, "E79.6", {"start": v(-54.26, 47.88) * mm, "mid": v(-58.44, 44.2) * mm, "end": v(-60, 38.83) * mm});
            skLineSegment(sketch, "E79.7", {"start": v(-60, 38.83) * mm, "end": v(-60, -38.83) * mm});
            skArc(sketch, "E79.8", {"start": v(-54.26, -47.88) * mm, "mid": v(0, -60) * mm, "end": v(54.26, -47.88) * mm});
            skArc(sketch, "E79.9", {"start": v(-60, -38.83) * mm, "mid": v(-58.44, -44.2) * mm, "end": v(-54.26, -47.88) * mm});
            skArc(sketch, "E79.10", {"start": v(54.26, -47.88) * mm, "mid": v(58.44, -44.2) * mm, "end": v(60, -38.83) * mm});
            skLineSegment(sketch, "E79.11", {"start": v(60, 38.83) * mm, "end": v(60, -38.83) * mm});
            skArc(sketch, "E79.12", {"start": v(60, 38.83) * mm, "mid": v(58.44, 44.2) * mm, "end": v(54.26, 47.88) * mm});
            skCircle(sketch, "E79.13", {"center": v(-60, 60) * mm, "radius": 4 * mm});
            skCircle(sketch, "E79.14", {"center": v(60, 60) * mm, "radius": 4 * mm});
            skCircle(sketch, "E79.15", {"center": v(60, -60) * mm, "radius": 4 * mm});
            skCircle(sketch, "E79.16", {"center": v(-60, -60) * mm, "radius": 4 * mm});
            skArc(sketch, "E79.17", {"start": v(54.26, 47.88) * mm, "mid": v(0, 60) * mm, "end": v(-54.26, 47.88) * mm});
            skArc(sketch, "E79.18", {"start": v(-64.25, 74.25) * mm, "mid": v(-71.32, 71.32) * mm, "end": v(-74.25, 64.25) * mm});
            skLineSegment(sketch, "E79.19", {"start": v(-64.25, 74.25) * mm, "end": v(64.25, 74.25) * mm});
            skPoint(sketch, "E79.20", {"position": v(71.32, -71.32) * mm});
            skLineSegment(sketch, "E80", {"start": v(0, 74.25) * mm, "end": v(0, 104.25) * mm, "construction": true});
            skLineSegment(sketch, "E81", {"start": v(-33, 74.25) * mm, "end": v(-15, 92.25) * mm});
            skLineSegment(sketch, "E82", {"start": v(33, 74.25) * mm, "end": v(15, 92.25) * mm});
            skLineSegment(sketch, "E83", {"start": v(-15, 92.25) * mm, "end": v(-15, 104.25) * mm});
            skLineSegment(sketch, "E84", {"start": v(15, 92.25) * mm, "end": v(15, 104.25) * mm});
            skArc(sketch, "E85", {"start": v(15, 104.25) * mm, "mid": v(0, 119.25) * mm, "end": v(-15, 104.25) * mm});
            skCircle(sketch, "E86", {"center": v(0, 104.25) * mm, "radius": 6 * mm});
            skLineSegment(sketch, "E87", {"start": v(-33, -74.25) * mm, "end": v(-15, -92.25) * mm});
            skLineSegment(sketch, "E88", {"start": v(33, -74.25) * mm, "end": v(15, -92.25) * mm});
            skLineSegment(sketch, "E89", {"start": v(-15, -92.25) * mm, "end": v(-15, -104.25) * mm});
            skLineSegment(sketch, "E90", {"start": v(15, -92.25) * mm, "end": v(15, -104.25) * mm});
            skArc(sketch, "E91", {"start": v(-15, -104.25) * mm, "mid": v(0, -119.25) * mm, "end": v(15, -104.25) * mm});
            skCircle(sketch, "E92", {"center": v(0, -104.25) * mm, "radius": 6 * mm});
            skLineSegment(sketch, "E93", {"start": v(0, -104.25) * mm, "end": v(0, -74.25) * mm, "construction": true});
            skSolve(sketch);
        }
        {
            var Q0;
            Q0 = qSketchRegion(id + "F16", true);
            var Q1;
            Q1=makeQuery(id+"F2.opExtrude","CAP_FACE",FACE,{"disambiguationData":[OSD([sQuery(id+"F0.wireOp",EDGE,"E12"),sQuery(id+"F0.wireOp",EDGE,"E13"),sQuery(id+"F0.wireOp",EDGE,"E14"),sQuery(id+"F0.wireOp",EDGE,"E15"),sQuery(id+"F0.wireOp",EDGE,"E17.filletArc"),sQuery(id+"F0.wireOp",EDGE,"E18.filletArc"),sQuery(id+"F0.wireOp",EDGE,"E19.filletArc"),sQuery(id+"F0.wireOp",EDGE,"E20.filletArc"),sQuery(id+"F0.wireOp",EDGE,"E25.0"),sQuery(id+"F0.wireOp",EDGE,"E25.1"),sQuery(id+"F0.wireOp",EDGE,"E25.2"),sQuery(id+"F0.wireOp",EDGE,"E25.3"),sQuery(id+"F0.wireOp",EDGE,"E25.4"),sQuery(id+"F0.wireOp",EDGE,"E25.5"),sQuery(id+"F0.wireOp",EDGE,"E25.6"),sQuery(id+"F0.wireOp",EDGE,"E25.7")])],"isStart":false});
            extrude(context, id + "F17", {"entities" : qUnion([Q0]), "endBound" : BoundingType.UP_TO_SURFACE, "endBoundEntityFace" : qUnion([Q1]), "depth" : 180 * mm, "offsetDistance" : 25 * mm});
        }
    });
